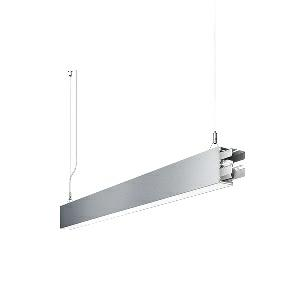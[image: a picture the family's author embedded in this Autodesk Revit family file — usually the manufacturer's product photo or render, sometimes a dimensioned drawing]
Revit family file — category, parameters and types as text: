
# Revit family: dotoo_line_-_dlp_1500_830_d_sta_00805844_bf51
name_source: partatom
category: Lighting Fixtures
units: mm (PartAtom-declared; Revit-internal decimal feet)

## family parameters
Cut with Voids When Loaded = No
Host = Face
Light Source = No
Part Type = Normal
Room Calculation Point = No
Round Connector Dimension = Use Diameter
Shared = No

## types (1)
- DOTOO.line - DLP 1500/830/D STA (1 x LED, 1300 lm, 3000K)
    Apparent Load = 13 VA
    Approval mark = CE
    CIE Flux Codes = 67 91 98 100 100
    Color Rendering = 80-89
    Color Temperature = 3000K
    Control Gear = Electronic ballast
    Default Elevation = 1800 mm
    Description = DLP 1500/830/D|Suspended luminaire|light source: LED|connected load: 220-240 V, 50/60 Hz|Power consumption: approx. 13 W|standby: approx. 0,20|luminous flux: 1300 lm|luminous efficacy: 100 lm/W|light distribution: Direct|direct ratio: approx. 100 %|colour temperature: Warm white, ca. 3000 K|color rendering index (CRI): >= 80|chromaticity tolerance:  3 SDCM|System of protection: IP 40|technology: Continuously dimmable|luminaire body|material: Sectional aluminium|colour: Silver|lamp cover: Acrylic (PMMA), Clear|mains lead: 2.00 m With free stranded wires|Fastening: Steel cable 0.3 - 0.7 m|glare control: Prism aperture|luminance(L65): <= 3000 cd/m|unified glare rating(4H 8H): <=  19|special features: DALI Load 1x, TouchDIM - dimming via standard switch, Through-wired, up to 18 m on one mains connection, Flicker-free, Suitable as emergency lighting, Start luminaire with mains connection, Mechanical and electrical connection of the individual modules without tools|
    Frequency = 50 Hz
    Height = 110 mm
    Lamp = 1 x LED
    Lamp Light Flux = 1300 lm
    Lamp count = 1
    Length = 1128 mm
    Luminous efficacy = 100 lm/W
    Manufacturer = Waldmann
    ModVariant = No
    Model = 00805844
    Mounting Place = Ceiling
    Mounting Type = Pendant
    Number of Poles = 1
    OnlyDefault = Yes
    Power Factor = 1
    Product Name = DOTOO.line - DLP 1500/830/D STA
    Product group = Suspended luminaire
    ProductGroupID = 9
    Protection Class = Protection class I
    Protection Degree = IP 40
    RLX_Detail_Level = 1
    RLX_Emergency_Light_Flux = 0 lm
    RLX_Emergency_Type = 0
    RLX_Emergency_Type_DB = No
    RlxData = <blob elided: 22473 chars, md5=0f35ee93>
    Socket = socket
    Standby Power = 0 W
    System Light Flux = 1300 lm
    System Power = 13 W
    Type Comments = Product without accessories
    Type Image = 113304000-00692576.jpg
    URL = http://relux.com
    VarID = ---
    Voltage = 230 V
    Voltage Range = 220-240 V
    Weight = 0.00 kg
    Width = 60 mm  [stored 0.19685 ft]

note: [stored X ft] marks values corroborated as IEEE doubles in the binary element streams (Revit-internal decimal feet)

## geometry (parser evidence)
native form markers: Blend x4, Sweep x13
no freeform markers — native parametric forms only
